# Revit family: ET AL_SNAP_1100
name_source: partatom
category: Furniture
units: mm (PartAtom-declared; Revit-internal decimal feet)

## family parameters
Always vertical = No
Cut with Voids When Loaded = No
OmniClass Number = 23.40.20.00
OmniClass Title = General Furniture and Specialties
Room Calculation Point = Yes
Shared = No
Work Plane-Based = No

## types (1)
- 48x50x78cm
    BIM BADGE = https://bim.archiproducts.com
    COLLECTION = Snap
    DEPTH = 500 mm  [stored 1.64042 ft]
    Description = Snap 1100 is a chair with steel frame, 4 legs.‎ Polypropylene shell.‎

Snap is a project consisting of a combination of polypropylene and steel pipes that create a seat, with and without armrests, and a stool that together represent the essence of sitting in its exemplary simplicity and functionality.‎
The seat has an atypical shell, made up of a plastic seat and back rest joined together by two ogival section arms, to allow movement making the seat structurally and aesthetically flexible and light.‎
The seat can be customized in a wide range of strong and contemporary colours, perfect for refined and dynamic interior and exterior projects and for large contract environments, such as meeting rooms, cafés and corporate catering venues.‎
The seat has an atypical shell, made up of a plastic seat and back rest joined together by two ogival section arms, to allow movement making the seat structurally and aesthetically flexible and light.‎
The seat can be customized in a wide range of strong and contemporary colours, perfect for refined and dynamic interior and exterior projects and for large contract environments, such as meeting rooms, cafés and corporate catering venues.‎
Composed by a chair, armchair and a stool, Classy is the result of an exemplary alchemy between functional elements and a particular aesthetic that together are found in the shell distinctive sign, gently modeled to ensure the highest standards of comfort and ergonomics.‎
The shape is a light, elegant and elastic sign, made even more evident by the play of contrasts of the alternation of matt and glossy surfaces.‎
    FRAME MATERIAL = ET AL_STEEL_CR_CHROME
    HEIGHT = 780 mm  [stored 2.55906 ft]
    MATERIAL DESCRIPTION = Frame: steel  Shell: Polypropylene
    Manufacturer = Et al.
    Model = Snap 1100
    PRODUCT SHEET = https://www.archiproducts.com
    SEAT HEIGHT = 470 mm  [stored 1.54199 ft]
    SEAT MATERIAL = ET AL_POLYPROPYLENE_WATER_BLUE
    TECHNICAL SHEET = https://www.et-al.it
    URL = https://www.et-al.it
    WEIGHT = 4.10 kg
    WIDTH = 480 mm  [stored 1.5748 ft]

note: [stored X ft] marks values corroborated as IEEE doubles in the binary element streams (Revit-internal decimal feet)

## geometry (parser evidence)
native form markers: Sweep x2
no freeform markers — native parametric forms only
